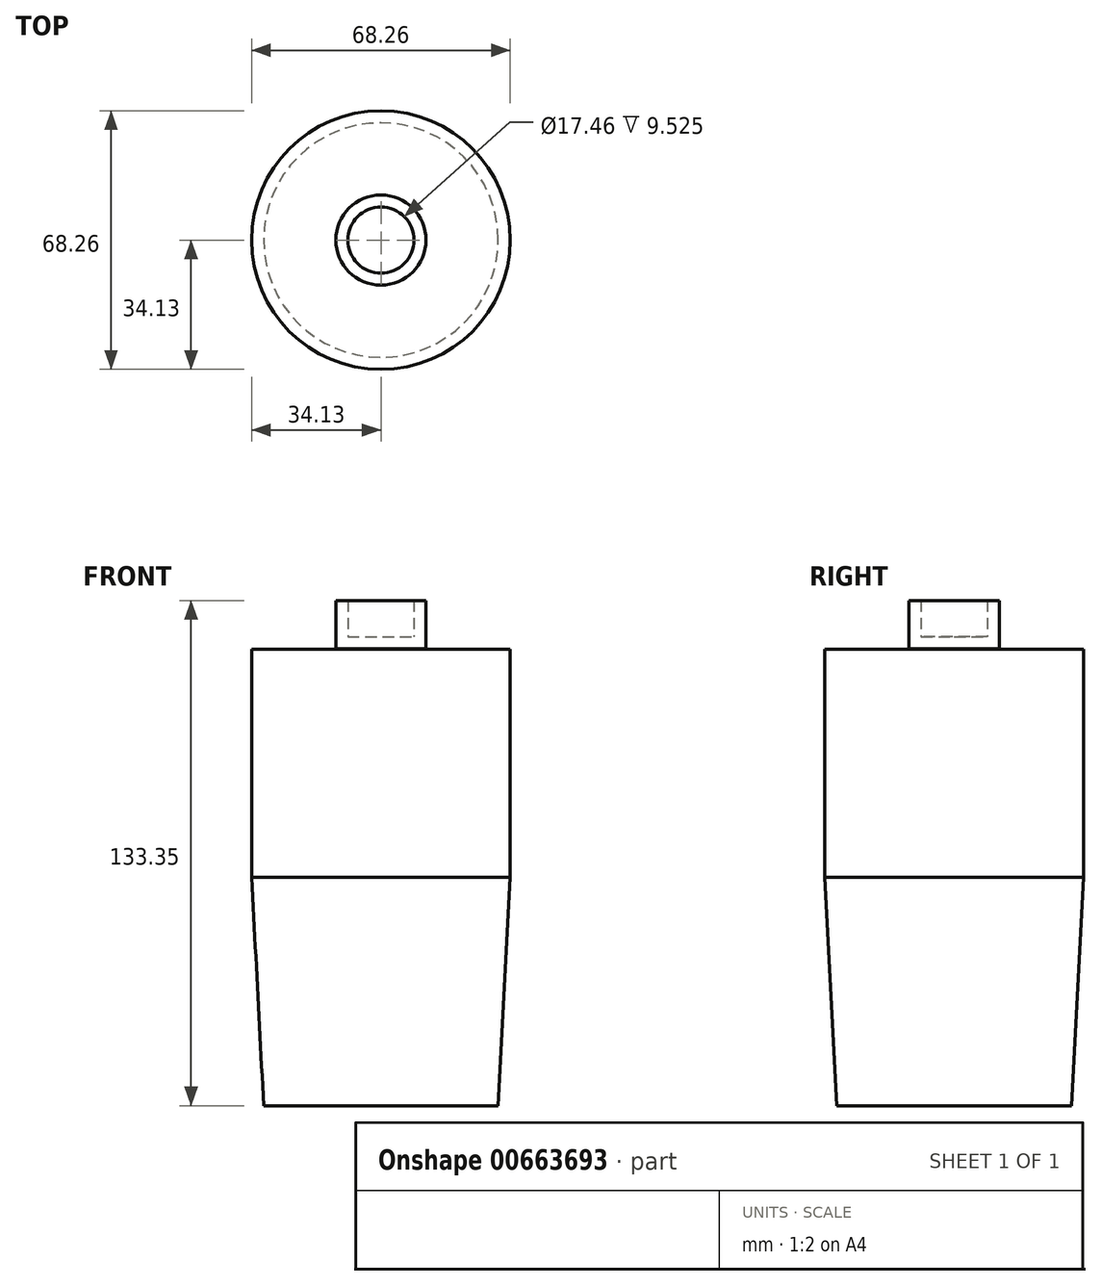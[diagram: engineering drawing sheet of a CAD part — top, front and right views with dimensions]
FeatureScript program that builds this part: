
annotation { "Feature Type Name" : "Feature", "Feature Type Description" : "" }
export const myFeature = defineFeature(function(context is Context, id is Id, definition is map)
    precondition{}
    {
        {
            var Q0;
            Q0=qCreatedBy(makeId("Front.planeOp"),FACE);
            var sketch = newSketch(context, id + "F0", { "sketchPlane" : qUnion([Q0])});
            skLineSegment(sketch, "E0", {"start": v(0, 0) * mm, "end": v(30.96, 0) * mm});
            skLineSegment(sketch, "E1", {"start": v(0, 0) * mm, "end": v(0, 120.65) * mm});
            skLineSegment(sketch, "E2", {"start": v(0, 120.65) * mm, "end": v(37.3, 120.65) * mm});
            skLineSegment(sketch, "E3", {"start": v(30.96, 0) * mm, "end": v(37.3, 120.65) * mm});
            skLineSegment(sketch, "E4", {"start": v(0, 120.65) * mm, "end": v(0, 133.35) * mm});
            skLineSegment(sketch, "E5", {"start": v(0, 133.35) * mm, "end": v(11.9, 133.35) * mm});
            skLineSegment(sketch, "E6", {"start": v(11.9, 133.35) * mm, "end": v(11.9, 120.65) * mm});
            skLineSegment(sketch, "E7", {"start": v(30.96, 0) * mm, "end": v(34.13, 60.33) * mm});
            skLineSegment(sketch, "E8", {"start": v(34.13, 60.33) * mm, "end": v(0, 60.33) * mm});
            skSolve(sketch);
        }
        {
            var Q0;
            {var subQ0=sQuery(id+"F0.wireOp",EDGE,"E4");Q0=makeQuery(id+"F0.imprint","IMPRINT",FACE,{"disambiguationData":[TD([[makeQuery(id+"F0.imprint","IMPRINT",EDGE,{"derivedFrom":subQ0}),-1.0]])]});}
            var Q1;
            Q1=makeQuery(id+"F0.imprint","IMPRINT",FACE,{"disambiguationData":[TD([[makeQuery(id+"F0.imprint","IMPRINT",EDGE,{"derivedFrom":sQuery(id+"F0.wireOp",EDGE,"E0")}),1.0]])]});
            var Q2;
            Q2=sQuery(id+"F0.wireOp",EDGE,"E1");
            revolve(context, id + "F1", {"entities" : qUnion([Q0, Q1]), "axis" : qUnion([Q2]), "revolveType" : RevolveType.FULL});
        }
        {
            var Q0;
            Q0=makeQuery(id+"F1.opRevolve","SWEPT_FACE",FACE,{"disambiguationData":[OSD([sQuery(id+"F0.wireOp",EDGE,"E5")])]});
            shell(context, id + "F2", {"entities" : qUnion([Q0]), "thickness" : 3.17 * mm});
        }
        {
            var Q0;
            Q0=makeQuery(id+"F1.opRevolve","SWEPT_FACE",FACE,{"disambiguationData":[OSD([sQuery(id+"F0.wireOp",EDGE,"E8")])]});
            extrude(context, id + "F3", {"entities" : qUnion([Q0]), "operationType" : NewBodyOperationType.ADD, "depth" : 60.2 * mm, "offsetDistance" : 25.4 * mm});
        }
    });
